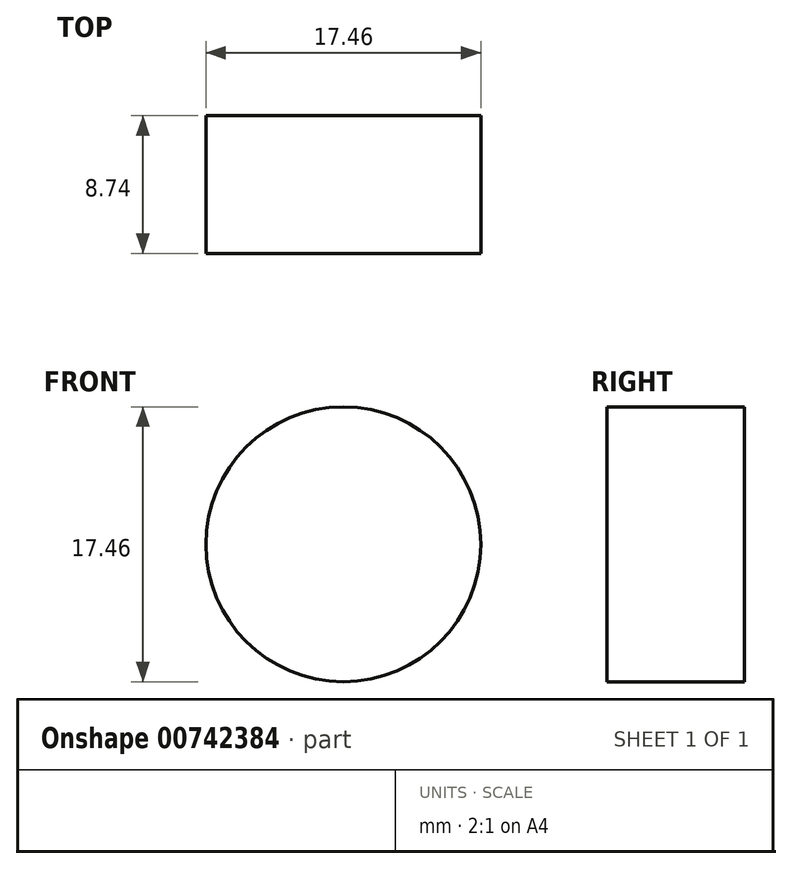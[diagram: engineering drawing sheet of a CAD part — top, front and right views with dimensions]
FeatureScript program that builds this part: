
annotation { "Feature Type Name" : "Feature", "Feature Type Description" : "" }
export const myFeature = defineFeature(function(context is Context, id is Id, definition is map)
    precondition{}
    {
        {
            var Q0;
            Q0=qCreatedBy(makeId("Front.planeOp"),FACE);
            var sketch = newSketch(context, id + "F0", { "sketchPlane" : qUnion([Q0])});
            skCircle(sketch, "E0", {"center": v(0, 0) * mm, "radius": 8.73 * mm});
            skSolve(sketch);
        }
        {
            var Q0;
            Q0=makeQuery(id+"F0.imprint","IMPRINT",FACE,{"disambiguationData":[TD([[makeQuery(id+"F0.imprint","IMPRINT",EDGE,{"derivedFrom":sQuery(id+"F0.wireOp",EDGE,"E0")}),1.0]])]});
            extrude(context, id + "F1", {"entities" : qUnion([Q0]), "depth" : 8.74 * mm, "offsetDistance" : 25.4 * mm});
        }
    });
